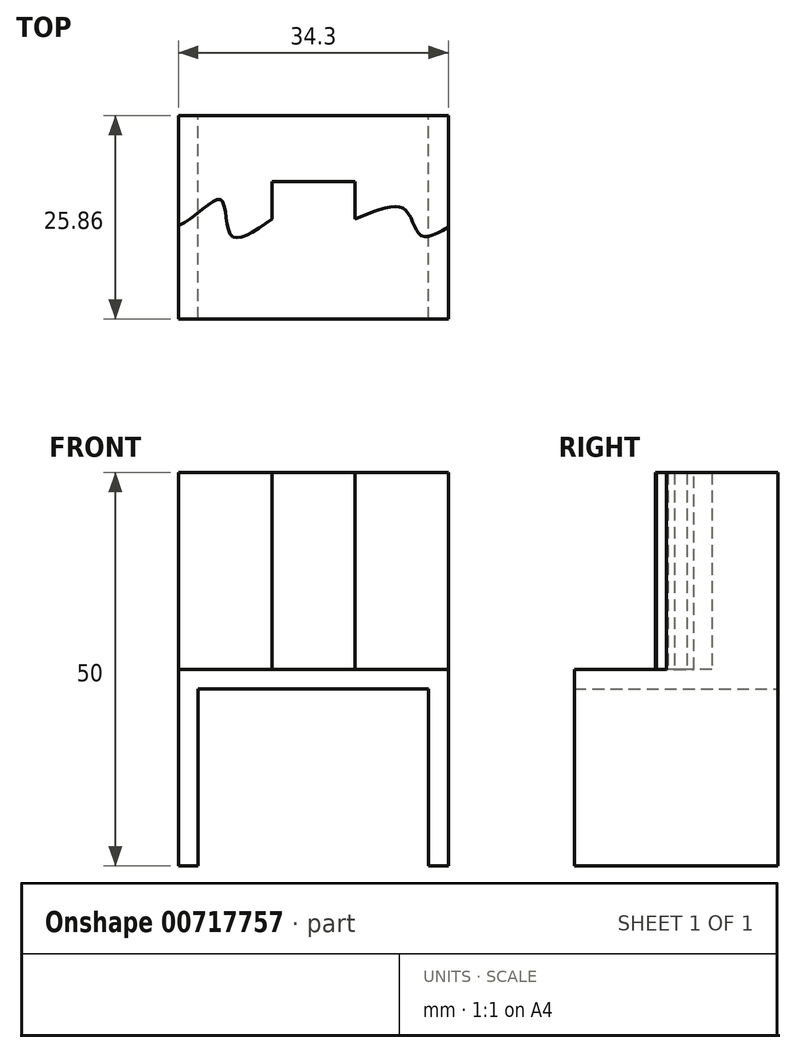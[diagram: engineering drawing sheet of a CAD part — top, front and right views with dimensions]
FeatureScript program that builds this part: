
annotation { "Feature Type Name" : "Feature", "Feature Type Description" : "" }
export const myFeature = defineFeature(function(context is Context, id is Id, definition is map)
    precondition{}
    {
        {
            var Q0;
            Q0=qCreatedBy(makeId("Top.planeOp"),FACE);
            var sketch = newSketch(context, id + "F0", { "sketchPlane" : qUnion([Q0])});
            skLineSegment(sketch, "E0.bottom", {"start": v(1.36, 0) * mm, "end": v(35.66, 0) * mm});
            skLineSegment(sketch, "E0.top", {"start": v(1.36, 25.86) * mm, "end": v(35.66, 25.86) * mm});
            skLineSegment(sketch, "E0.left", {"start": v(1.36, 0) * mm, "end": v(1.36, 25.86) * mm});
            skLineSegment(sketch, "E0.right", {"start": v(35.66, 0) * mm, "end": v(35.66, 25.86) * mm});
            skSolve(sketch);
        }
        {
            var Q0;
            Q0 = qSketchRegion(id + "F0", true);
            extrude(context, id + "F1", {"entities" : qUnion([Q0]), "depth" : 25 * mm, "offsetDistance" : 25 * mm});
        }
        {
            var Q0;
            Q0=makeQuery(id+"F1.opExtrude","SWEPT_FACE",FACE,{"disambiguationData":[OSD([sQuery(id+"F0.wireOp",EDGE,"E0.top")])]});
            var Q1;
            Q1=makeQuery(id+"F1.opExtrude","SWEPT_FACE",FACE,{"disambiguationData":[OSD([sQuery(id+"F0.wireOp",EDGE,"E0.bottom")])]});
            var Q2;
            Q2=makeQuery(id+"F1.opExtrude","CAP_FACE",FACE,{"disambiguationData":[OSD([sQuery(id+"F0.wireOp",EDGE,"E0.bottom"),sQuery(id+"F0.wireOp",EDGE,"E0.top"),sQuery(id+"F0.wireOp",EDGE,"E0.left"),sQuery(id+"F0.wireOp",EDGE,"E0.right")])],"isStart":true});
            shell(context, id + "F2", {"entities" : qUnion([Q0, Q1, Q2]), "thickness" : 2.5 * mm});
        }
        {
            var Q0;
            Q0=makeQuery(id+"F1.opExtrude","CAP_FACE",FACE,{"disambiguationData":[OSD([sQuery(id+"F0.wireOp",EDGE,"E0.bottom"),sQuery(id+"F0.wireOp",EDGE,"E0.top"),sQuery(id+"F0.wireOp",EDGE,"E0.left"),sQuery(id+"F0.wireOp",EDGE,"E0.right")])],"isStart":false});
            var sketch = newSketch(context, id + "F3", { "sketchPlane" : qUnion([Q0])});
            skLineSegment(sketch, "E1.bottom", {"start": v(23.8, 17.46) * mm, "end": v(13.26, 17.46) * mm});
            skLineSegment(sketch, "E1.top", {"start": v(23.8, 7.92) * mm, "end": v(13.26, 7.92) * mm});
            skLineSegment(sketch, "E1.left", {"start": v(23.8, 17.46) * mm, "end": v(23.8, 7.92) * mm});
            skLineSegment(sketch, "E1.right", {"start": v(13.26, 17.46) * mm, "end": v(13.26, 7.92) * mm});
            skFitSpline(sketch, "E2", {"points": [v(23.8, 12.69) * mm, v(30.15, 13.9) * mm, v(32.2, 10.62) * mm, v(39.5, 14.63) * mm], "startDerivative": vector(22.33, 9.59) * mm, "endDerivative": vector(22.88, 18.4) * mm});
            skFitSpline(sketch, "E3", {"points": [v(13.26, 12.69) * mm, v(8.05, 10.66) * mm, v(6.77, 15.14) * mm, v(1.36, 11.86) * mm, v(-4.42, 13.44) * mm], "startDerivative": vector(-26.16, -18.41) * mm, "endDerivative": vector(-21.54, 13.95) * mm});
            skSolve(sketch);
        }
        {
            var Q0;
            {var subQ6=sQuery(id+"F3.wireOp",EDGE,"E1.bottom");Q0=makeQuery(id+"F3.imprint","IMPRINT",FACE,{"disambiguationData":[TD([[makeQuery(id+"F3.imprint","IMPRINT",EDGE,{"derivedFrom":subQ6}),-1.0]])]});}
            extrude(context, id + "F4", {"entities" : qUnion([Q0]), "operationType" : NewBodyOperationType.ADD, "depth" : 25 * mm, "offsetDistance" : 25 * mm});
        }
    });
